# Revit family: B 1000 SIL
name_source: partatom
category: Lighting Fixtures
revit_build: Autodesk Revit 2016 (Build: 20150714_1515(x64)
units: mm (PartAtom-declared; Revit-internal decimal feet)

## family parameters
Always vertical = Yes
Cut with Voids When Loaded = No
Light Source = Yes
OmniClass Number = 23.80.70.00
OmniClass Title = Lighting
Part Type = Normal
Room Calculation Point = No
Round Connector Dimension = Use Diameter
Shared = No
Work Plane-Based = No

## types (1)
- BSIL.1000.13.27
    Color Filter = 16777215
    Dimming Lamp Color Temperature Shift = <None>
    Emit Shape Visible in Rendering = Yes
    Emit from Circle Diameter = 140 mm  [stored 0.459318 ft]
    Light Source Symbol Size = 610 mm
    Manufacturer = ARLIGHT
    Type Image = B 1000 SIL.JPG
    Wattage Comments = 13

note: [stored X ft] marks values corroborated as IEEE doubles in the binary element streams (Revit-internal decimal feet)

## geometry (parser evidence)
native form markers: Sweep x3
no freeform markers — native parametric forms only
